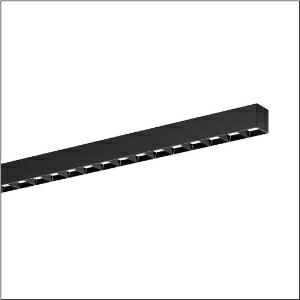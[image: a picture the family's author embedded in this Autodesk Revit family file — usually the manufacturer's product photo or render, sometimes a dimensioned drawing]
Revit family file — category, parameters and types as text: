
# Revit family: silica_21_51mx24dc3abb
name_source: partatom
category: Lighting Fixtures
units: mm (PartAtom-declared; Revit-internal decimal feet)

## family parameters
Cut with Voids When Loaded = No
Host = Face
Light Source = No
Part Type = Normal
Room Calculation Point = No
Round Connector Dimension = Use Diameter
Shared = No

## types (1)
- --- (1 x LED, 10800 lm, 79 W, 3000K)
    Apparent Load = 79 VA
    CIE Flux Codes = 74 94 99 100 100
    Color Rendering = 80
    Color Temperature = 3000K
    Default Elevation = 1800 mm
    Description = Silica 21, office luminaire, primary light control with darklight reflector, of PMMA, black, CAT 2 (L<= 3000cd/m²), light emission: direct distribution, primary light characteristic: asymmetric, installation type: surface-mounted, LED, rated luminous flux: 10.800lm, luminous efficacy: 137lm/W, light colour: 830, colour temperature: 3000K, control gear: DALI 2, with terminal, 3+2-pole, max. 2.5mm², mains connection: 220..240V, AC, 50/60Hz, rated input power: 79W, luminaire housing, of aluminium, matt jet black (RAL 9005), length: 3.004mm, width: 53mm, height: 53mm, protection rating (complete): IP20, insulation class (complete): insulation class I (protective earthing), certification: CE, permissible operating ambient temperature: 0..+35°C, standard: EN 50419, packaging unit: 1 piece
    Height = 53 mm
    Lamp = 1 x LED
    Lamp Light Flux = 10800 lm
    Lamp Power = 79 W
    Lamp count = 1
    Length = 3004 mm
    Luminous efficacy = 137 lm/W
    Manufacturer = Siteco
    ModVariant = No
    Model = 51MX24DC3ABB
    Mounting Place = Ceiling
    Mounting Type = Surface mounted
    Number of Poles = 1
    OnlyDefault = Yes
    Power Factor = 1
    Product Name = Silica 21
    Product group = office luminaire | ceiling mounted
    ProductGroupID = 301
    Protection Class = Protection class I
    Protection Degree = IP 20
    RLX_Detail_Level = 1
    RLX_Emergency_Light_Flux = 0 lm
    RLX_Emergency_Type = 0
    RLX_Emergency_Type_DB = No
    RlxData = <blob elided: 66437 chars, md5=864cc3a5>
    Socket = socket
    Standby Power = 0 W
    System Light Flux = 10800 lm
    System Power = 79 W
    Type Comments = factory setting: luminous flux: 100 % | dim-lin: 254 | 448 mA
    Type Image = l_1335908.jpg
    URL = http://relux.com
    VarID = @adj_124547
    Voltage = 0 V
    Weight = 0.00 kg
    Width = 53 mm

## geometry (parser evidence)
native form markers: Blend x4, Sweep x11
no freeform markers — native parametric forms only
